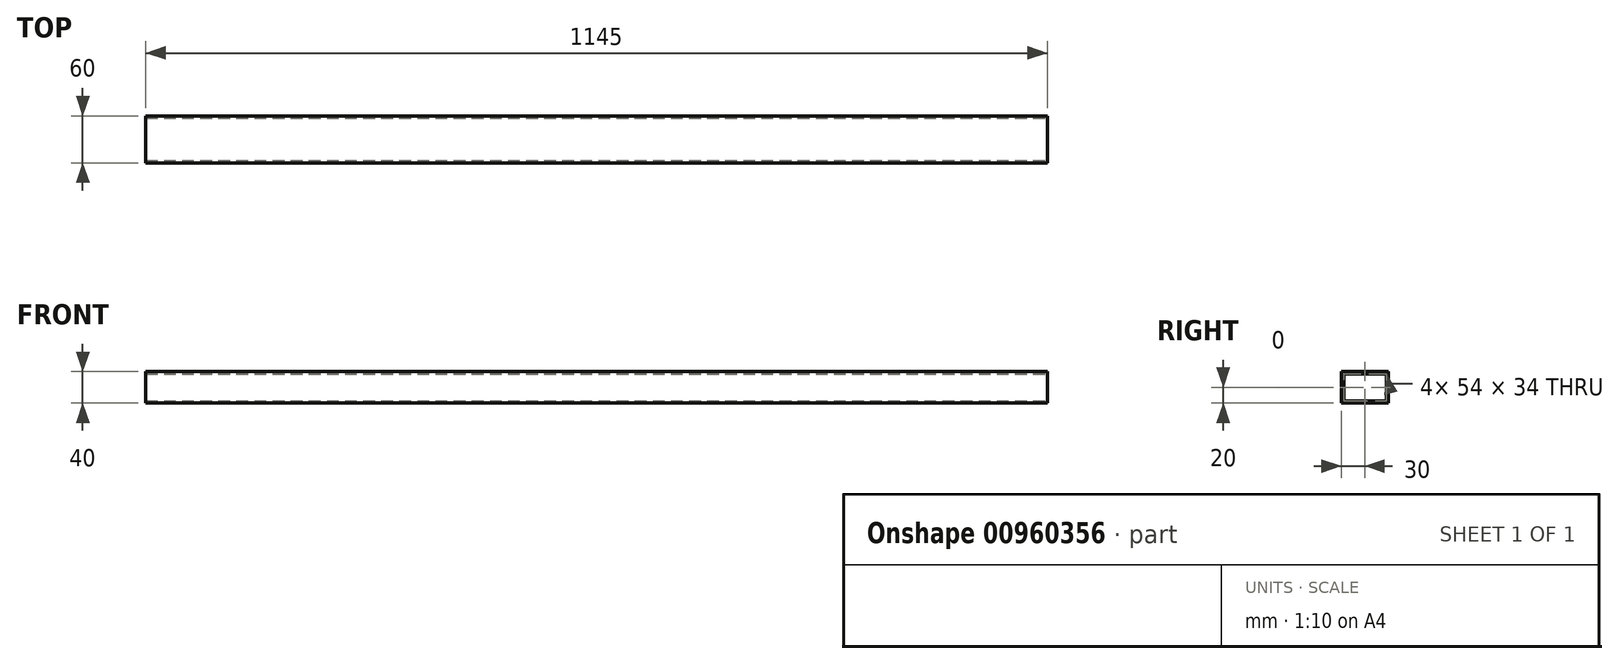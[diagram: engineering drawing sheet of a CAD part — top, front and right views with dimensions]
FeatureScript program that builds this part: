
annotation { "Feature Type Name" : "Feature", "Feature Type Description" : "" }
export const myFeature = defineFeature(function(context is Context, id is Id, definition is map)
    precondition{}
    {
        {
            var Q0;
            Q0=qCreatedBy(makeId("Top.planeOp"),FACE);
            var sketch = newSketch(context, id + "F0", { "sketchPlane" : qUnion([Q0])});
            skLineSegment(sketch, "E0.bottom", {"start": v(-572.5, 30) * mm, "end": v(572.5, 30) * mm});
            skLineSegment(sketch, "E0.top", {"start": v(-572.5, -30) * mm, "end": v(572.5, -30) * mm});
            skLineSegment(sketch, "E0.left", {"start": v(-572.5, 30) * mm, "end": v(-572.5, -30) * mm});
            skLineSegment(sketch, "E0.right", {"start": v(572.5, 30) * mm, "end": v(572.5, -30) * mm});
            skPoint(sketch, "E0.middle", {"position": v(0, 0) * mm});
            skSolve(sketch);
        }
        {
            var Q0;
            Q0 = qSketchRegion(id + "F0", true);
            extrude(context, id + "F1", {"entities" : qUnion([Q0]), "depth" : 40 * mm, "offsetDistance" : 25 * mm});
        }
        {
            var Q0;
            Q0=makeQuery(id+"F1.opExtrude","SWEPT_FACE",FACE,{"disambiguationData":[OSD([sQuery(id+"F0.wireOp",EDGE,"E0.left")])]});
            var Q1;
            Q1=makeQuery(id+"F1.opExtrude","SWEPT_FACE",FACE,{"disambiguationData":[OSD([sQuery(id+"F0.wireOp",EDGE,"E0.right")])]});
            shell(context, id + "F2", {"entities" : qUnion([Q0, Q1]), "thickness" : 3 * mm});
        }
    });
